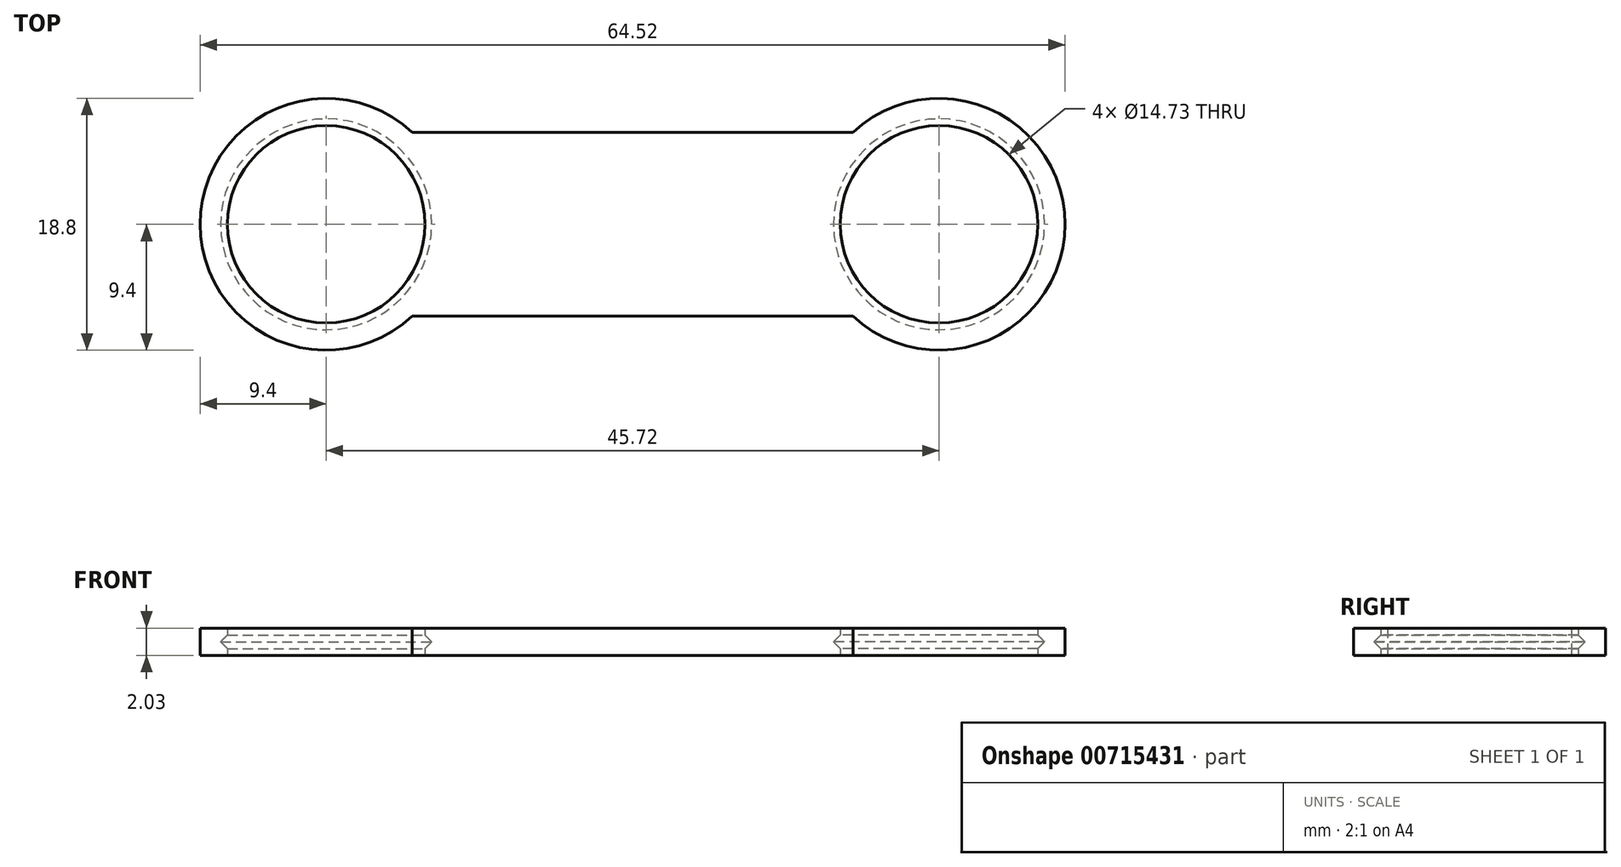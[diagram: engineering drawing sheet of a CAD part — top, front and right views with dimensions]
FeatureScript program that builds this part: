
annotation { "Feature Type Name" : "Feature", "Feature Type Description" : "" }
export const myFeature = defineFeature(function(context is Context, id is Id, definition is map)
    precondition{}
    {
        {
            var Q0;
            Q0=qCreatedBy(makeId("Top.planeOp"),FACE);
            var sketch = newSketch(context, id + "F0", { "sketchPlane" : qUnion([Q0])});
            skCircle(sketch, "E0", {"center": v(-22.86, 0) * mm, "radius": 8.13 * mm});
            skCircle(sketch, "E1", {"center": v(22.86, 0) * mm, "radius": 8.13 * mm});
            skLineSegment(sketch, "E2", {"start": v(-18.5, -6.86) * mm, "end": v(18.5, -6.86) * mm});
            skLineSegment(sketch, "E3", {"start": v(-18.5, 6.86) * mm, "end": v(18.5, 6.86) * mm});
            skPoint(sketch, "E4", {"position": v(0, -6.86) * mm});
            skSolve(sketch);
        }
        {
            var Q0;
            {var subQ0=sQuery(id+"F0.wireOp",EDGE,"E2");Q0=makeQuery(id+"F0.imprint","IMPRINT",FACE,{"disambiguationData":[TD([[makeQuery(id+"F0.imprint","IMPRINT",EDGE,{"derivedFrom":subQ0}),1.0]])]});}
            extrude(context, id + "F1", {"entities" : qUnion([Q0]), "depth" : 2.03 * mm, "offsetDistance" : 25.4 * mm});
        }
        {
            var Q0;
            Q0=qCreatedBy(makeId("Front.planeOp"),FACE);
            var sketch = newSketch(context, id + "F2", { "sketchPlane" : qUnion([Q0])});
            skLineSegment(sketch, "E5", {"start": v(-22.86, 0) * mm, "end": v(-22.86, 1.83) * mm});
            skLineSegment(sketch, "E6", {"start": v(-32.26, 0) * mm, "end": v(-32.26, 2.03) * mm});
            skLineSegment(sketch, "E7", {"start": v(-32.26, 2.03) * mm, "end": v(-30.23, 2.03) * mm});
            skLineSegment(sketch, "E8", {"start": v(-30.23, 2.03) * mm, "end": v(-30.23, 1.52) * mm});
            skLineSegment(sketch, "E9", {"start": v(-30.23, 1.52) * mm, "end": v(-30.73, 1.02) * mm});
            skLineSegment(sketch, "E10", {"start": v(-30.73, 1.02) * mm, "end": v(-30.23, 0.5) * mm});
            skLineSegment(sketch, "E11", {"start": v(-30.23, 0.5) * mm, "end": v(-30.23, 0) * mm});
            skLineSegment(sketch, "E12", {"start": v(-32.26, 0) * mm, "end": v(-30.23, 0) * mm});
            skLineSegment(sketch, "E13", {"start": v(-22.86, 0) * mm, "end": v(-32.26, 0) * mm});
            skSolve(sketch);
        }
        {
            var Q0;
            Q0=makeQuery(id+"F2.imprint","IMPRINT",FACE,{"disambiguationData":[TD([[makeQuery(id+"F2.imprint","IMPRINT",EDGE,{"derivedFrom":sQuery(id+"F2.wireOp",EDGE,"E6")}),-1.0]])]});
            var Q1;
            Q1=sQuery(id+"F2.wireOp",EDGE,"E5");
            revolve(context, id + "F3", {"operationType" : NewBodyOperationType.ADD, "surfaceOperationType" : NewSurfaceOperationType.NEW, "entities" : qUnion([Q0]), "axis" : qUnion([Q1]), "revolveType" : RevolveType.FULL});
        }
        {
            var Q0;
            Q0=makeQuery(id+"F1.opExtrude","SWEPT_BODY",BODY,{"disambiguationData":[OSD([sQuery(id+"F0.wireOp",EDGE,"E0"),sQuery(id+"F0.wireOp",EDGE,"E1"),sQuery(id+"F0.wireOp",EDGE,"E2"),sQuery(id+"F0.wireOp",EDGE,"E3")])]});
            var Q1;
            Q1=qCreatedBy(makeId("Right.planeOp"),FACE);
            mirror(context, id + "F4", {"operationType" : NewBodyOperationType.ADD, "entities" : qUnion([Q0]), "mirrorPlane" : qUnion([Q1])});
        }
    });
